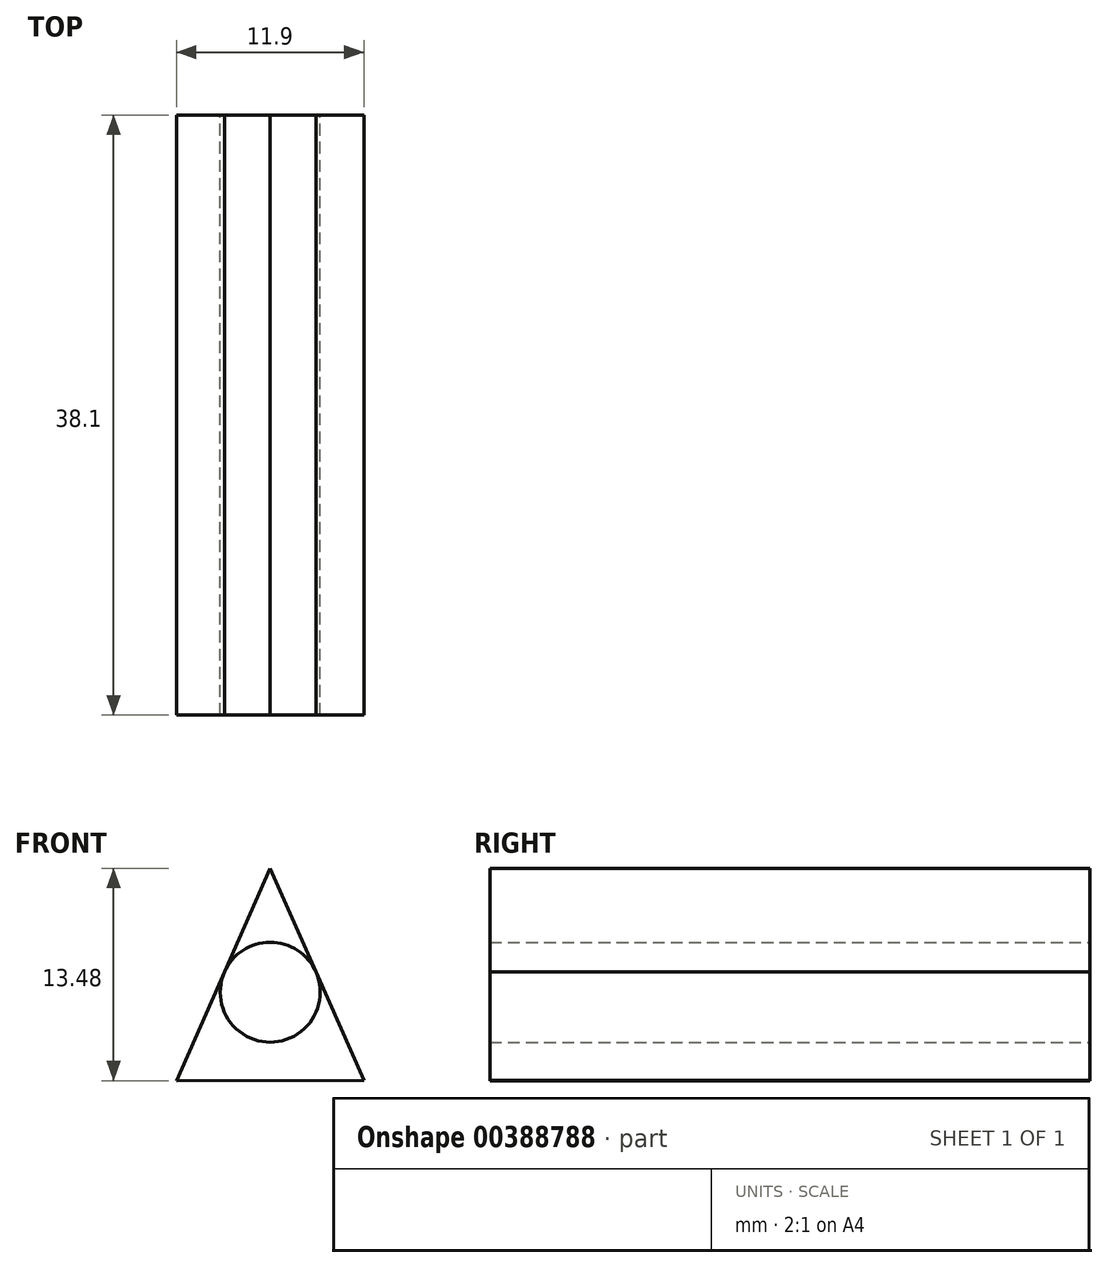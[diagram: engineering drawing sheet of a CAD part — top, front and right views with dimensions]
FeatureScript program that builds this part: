
annotation { "Feature Type Name" : "Feature", "Feature Type Description" : "" }
export const myFeature = defineFeature(function(context is Context, id is Id, definition is map)
    precondition{}
    {
        {
            var Q0;
            Q0=qCreatedBy(makeId("Front.planeOp"),FACE);
            var sketch = newSketch(context, id + "F0", { "sketchPlane" : qUnion([Q0])});
            skCircle(sketch, "E0", {"center": v(0, 0) * mm, "radius": 3.18 * mm});
            skLineSegment(sketch, "E1", {"start": v(0, 7.86) * mm, "end": v(-5.95, -5.62) * mm});
            skLineSegment(sketch, "E2", {"start": v(0, 7.86) * mm, "end": v(5.95, -5.61) * mm});
            skLineSegment(sketch, "E3", {"start": v(5.95, -5.61) * mm, "end": v(-5.95, -5.62) * mm});
            skSolve(sketch);
        }
        {
            var Q0;
            {var subQ5=sQuery(id+"F0.wireOp",EDGE,"E3");Q0=makeQuery(id+"F0.imprint","IMPRINT",FACE,{"disambiguationData":[TD([[makeQuery(id+"F0.imprint","IMPRINT",EDGE,{"derivedFrom":subQ5}),-1.0]])]});}
            var Q1;
            {var subQ0=sQuery(id+"F0.wireOp",EDGE,"E1");var subQ1=sQuery(id+"F0.wireOp",EDGE,"E0");var subQ2=makeQuery(id+"F0.imprint","INTERSECT",VERTEX,{"derivedFrom":[subQ1,subQ0]});Q1=makeQuery(id+"F0.imprint","IMPRINT",FACE,{"disambiguationData":[TD([[makeQuery(id+"F0.imprint","IMPRINT",EDGE,{"disambiguationData":[TD([[subQ2,1.0]])],"derivedFrom":subQ1}),-1.0]])]});}
            extrude(context, id + "F1", {"entities" : qUnion([Q0, Q1]), "endBound" : BoundingType.SYMMETRIC, "depth" : 38.1 * mm});
        }
    });
